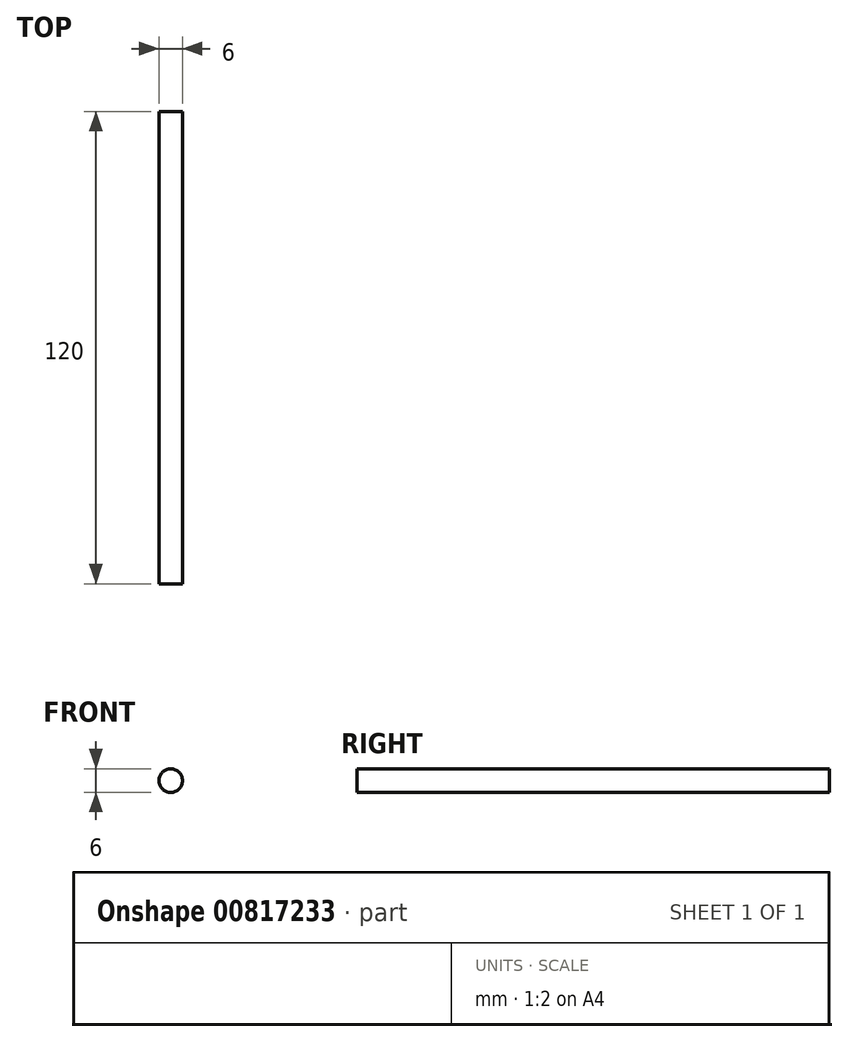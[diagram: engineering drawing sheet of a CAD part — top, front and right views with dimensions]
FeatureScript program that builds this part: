
annotation { "Feature Type Name" : "Feature", "Feature Type Description" : "" }
export const myFeature = defineFeature(function(context is Context, id is Id, definition is map)
    precondition{}
    {
        {
            var Q0;
            Q0=qCreatedBy(makeId("Front.planeOp"),FACE);
            var sketch = newSketch(context, id + "F0", { "sketchPlane" : qUnion([Q0])});
            skCircle(sketch, "E0", {"center": v(0, 0) * mm, "radius": 3 * mm});
            skSolve(sketch);
        }
        {
            var Q0;
            Q0 = qSketchRegion(id + "F0", true);
            extrude(context, id + "F1", {"entities" : qUnion([Q0]), "depth" : 120 * mm, "offsetDistance" : 25 * mm});
        }
    });
